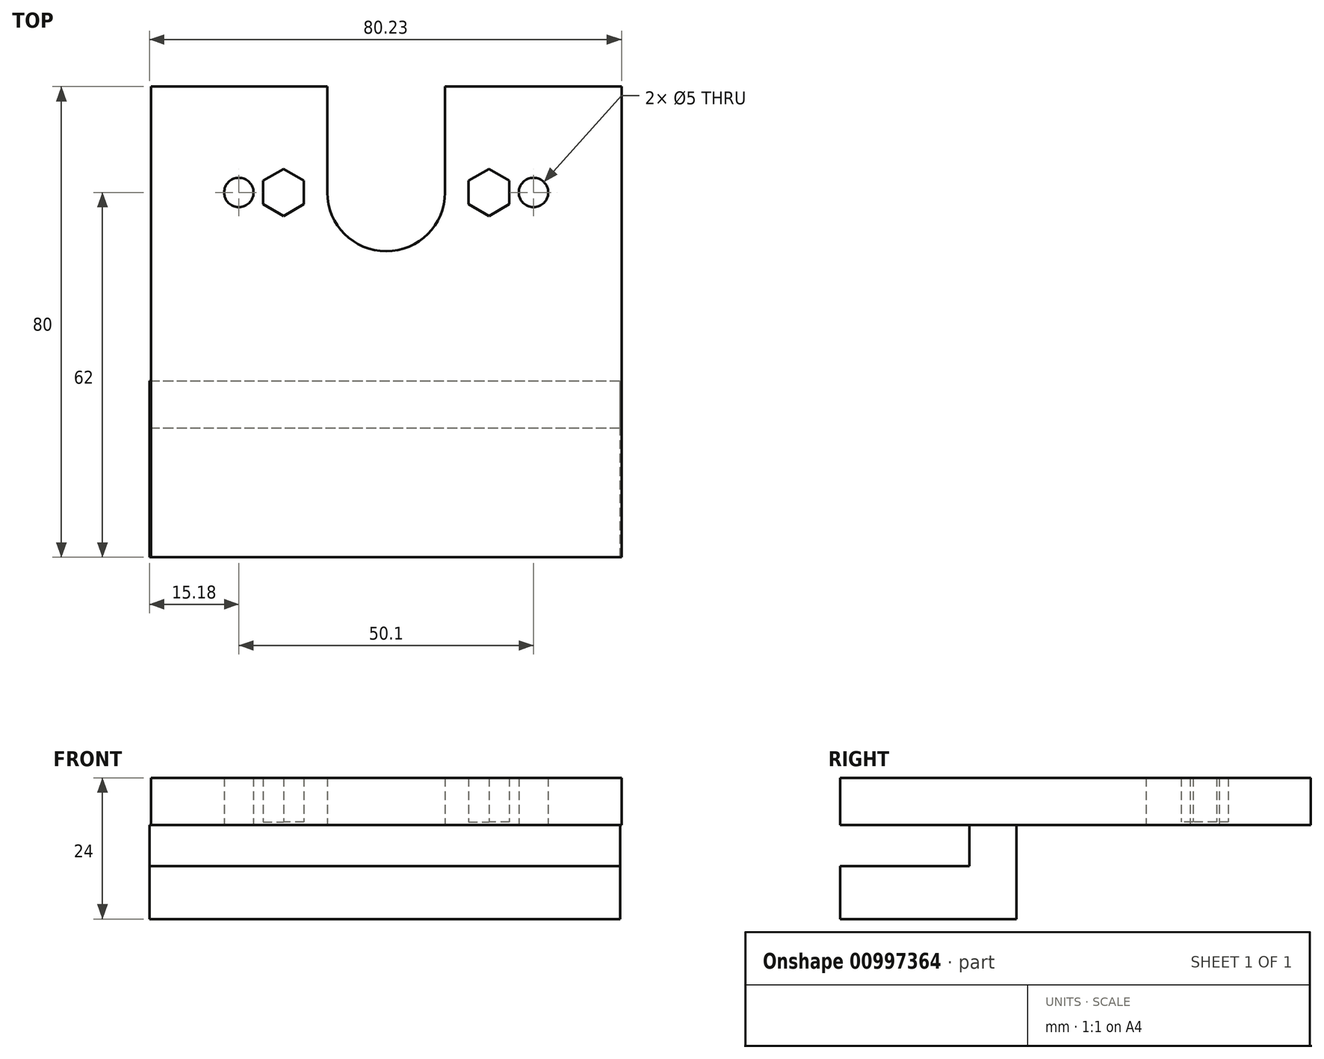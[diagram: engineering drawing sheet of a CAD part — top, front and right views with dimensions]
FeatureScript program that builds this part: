
annotation { "Feature Type Name" : "Feature", "Feature Type Description" : "" }
export const myFeature = defineFeature(function(context is Context, id is Id, definition is map)
    precondition{}
    {
        {
            var Q0;
            Q0=qCreatedBy(makeId("Top.planeOp"),FACE);
            var sketch = newSketch(context, id + "F0", { "sketchPlane" : qUnion([Q0])});
            skLineSegment(sketch, "E0.top", {"start": v(40.25, 40) * mm, "end": v(10, 40) * mm});
            skPoint(sketch, "E0.middle", {"position": v(0, 0) * mm});
            skLineSegment(sketch, "E1.MirrorCS", {"start": v(-40, 40) * mm, "end": v(-10, 40) * mm});
            skLineSegment(sketch, "E2", {"start": v(10, 40) * mm, "end": v(10, 22) * mm});
            skLineSegment(sketch, "E3.MirrorCS", {"start": v(-10, 40) * mm, "end": v(-10, 22) * mm});
            skArc(sketch, "E4", {"start": v(-10, 22) * mm, "mid": v(0, 12) * mm, "end": v(10, 22) * mm});
            skPoint(sketch, "E5", {"position": v(25.05, 22) * mm});
            skPoint(sketch, "E6", {"position": v(17.46, 22) * mm});
            skPoint(sketch, "E7.MirrorP", {"position": v(-17.46, 22) * mm});
            skPoint(sketch, "E8.MirrorP", {"position": v(-25.05, 22) * mm});
            skLineSegment(sketch, "E9", {"start": v(-40, 40) * mm, "end": v(-40, -40) * mm});
            skLineSegment(sketch, "E10.MirrorCS", {"start": v(40, 40) * mm, "end": v(40, -40) * mm});
            skLineSegment(sketch, "E11", {"start": v(-40, -40) * mm, "end": v(40, -40) * mm});
            skSolve(sketch);
        }
        {
            var Q0;
            Q0 = qSketchRegion(id + "F0", true);
            extrude(context, id + "F1", {"entities" : qUnion([Q0]), "depth" : 8 * mm, "offsetDistance" : 25 * mm});
        }
        {
            var Q0;
            Q0=sQuery(id+"F0.wireOp",VERTEX,"E5");
            var Q1;
            Q1=makeQuery(id+"F1.opExtrude","SWEPT_BODY",BODY,{"disambiguationData":[OSD([sQuery(id+"F0.wireOp",EDGE,"E0.top"),sQuery(id+"F0.wireOp",EDGE,"E1.MirrorCS"),sQuery(id+"F0.wireOp",EDGE,"E2"),sQuery(id+"F0.wireOp",EDGE,"E3.MirrorCS"),sQuery(id+"F0.wireOp",EDGE,"E4"),sQuery(id+"F0.wireOp",EDGE,"9f457f28-b589-4e44-85d8-e6faa38afad9"),sQuery(id+"F0.wireOp",EDGE,"d04040d8-0d85-434a-9426-19c5aca7a986"),sQuery(id+"F0.wireOp",EDGE,"XwE4FMA8-GxFN-yl6x-s7Xw-O0s0oBugfnyy")])]});
            hole(context, id + "F2", {"style" : HoleStyle.SIMPLE, "endStyle" : HoleEndStyle.THROUGH, "oppositeDirection" : true, "holeDiameter" : 5 * mm, "majorDiameter" : 5 * mm, "isTappedThrough" : true, "tappedDepth" : 12 * mm, "tapClearance" : 3, "startFromSketch" : true, "locations" : qUnion([Q0]), "scope" : qUnion([Q1])});
        }
        {
            var Q0;
            Q0=sQuery(id+"F0.wireOp",VERTEX,"E8.MirrorP");
            var Q1;
            Q1=makeQuery(id+"F1.opExtrude","SWEPT_BODY",BODY,{"disambiguationData":[OSD([sQuery(id+"F0.wireOp",EDGE,"E0.top"),sQuery(id+"F0.wireOp",EDGE,"E1.MirrorCS"),sQuery(id+"F0.wireOp",EDGE,"E2"),sQuery(id+"F0.wireOp",EDGE,"E3.MirrorCS"),sQuery(id+"F0.wireOp",EDGE,"E4"),sQuery(id+"F0.wireOp",EDGE,"9f457f28-b589-4e44-85d8-e6faa38afad9"),sQuery(id+"F0.wireOp",EDGE,"d04040d8-0d85-434a-9426-19c5aca7a986"),sQuery(id+"F0.wireOp",EDGE,"XwE4FMA8-GxFN-yl6x-s7Xw-O0s0oBugfnyy")])]});
            hole(context, id + "F3", {"style" : HoleStyle.SIMPLE, "endStyle" : HoleEndStyle.THROUGH, "oppositeDirection" : true, "holeDiameter" : 5 * mm, "majorDiameter" : 5 * mm, "isTappedThrough" : true, "tappedDepth" : 12 * mm, "tapClearance" : 3, "startFromSketch" : true, "locations" : qUnion([Q0]), "scope" : qUnion([Q1])});
        }
        {
            var Q0;
            Q0=makeQuery(id+"F1.opExtrude","CAP_FACE",FACE,{"disambiguationData":[OSD([sQuery(id+"F0.wireOp",EDGE,"E0.top"),sQuery(id+"F0.wireOp",EDGE,"E1.MirrorCS"),sQuery(id+"F0.wireOp",EDGE,"E2"),sQuery(id+"F0.wireOp",EDGE,"E3.MirrorCS"),sQuery(id+"F0.wireOp",EDGE,"E4"),sQuery(id+"F0.wireOp",EDGE,"9f457f28-b589-4e44-85d8-e6faa38afad9"),sQuery(id+"F0.wireOp",EDGE,"d04040d8-0d85-434a-9426-19c5aca7a986"),sQuery(id+"F0.wireOp",EDGE,"XwE4FMA8-GxFN-yl6x-s7Xw-O0s0oBugfnyy")])],"isStart":false});
            var sketch = newSketch(context, id + "F4", { "sketchPlane" : qUnion([Q0])});
            skCircle(sketch, "E12.cCircle", {"center": v(-17.46, 22) * mm, "radius": 3.46 * mm, "construction": true});
            skLineSegment(sketch, "E12.0", {"start": v(-14, 20) * mm, "end": v(-17.46, 18) * mm});
            skLineSegment(sketch, "E12.1", {"start": v(-17.46, 18) * mm, "end": v(-20.93, 20) * mm});
            skLineSegment(sketch, "E12.2", {"start": v(-20.93, 20) * mm, "end": v(-20.93, 24) * mm});
            skLineSegment(sketch, "E12.3", {"start": v(-20.93, 24) * mm, "end": v(-17.46, 26) * mm});
            skLineSegment(sketch, "E12.4", {"start": v(-17.46, 26) * mm, "end": v(-14, 24) * mm});
            skLineSegment(sketch, "E12.5", {"start": v(-14, 24) * mm, "end": v(-14, 20) * mm});
            skPoint(sketch, "E12.0.midPoint", {"position": v(-15.73, 19) * mm});
            skCircle(sketch, "E13.cCircle", {"center": v(17.46, 22) * mm, "radius": 3.46 * mm, "construction": true});
            skLineSegment(sketch, "E13.0", {"start": v(20.93, 20) * mm, "end": v(17.46, 18) * mm});
            skLineSegment(sketch, "E13.1", {"start": v(17.46, 18) * mm, "end": v(14, 20) * mm});
            skLineSegment(sketch, "E13.2", {"start": v(14, 20) * mm, "end": v(14, 24) * mm});
            skLineSegment(sketch, "E13.3", {"start": v(14, 24) * mm, "end": v(17.46, 26) * mm});
            skLineSegment(sketch, "E13.4", {"start": v(17.46, 26) * mm, "end": v(20.93, 24) * mm});
            skLineSegment(sketch, "E13.5", {"start": v(20.93, 24) * mm, "end": v(20.93, 20) * mm});
            skPoint(sketch, "E13.0.midPoint", {"position": v(19.2, 19) * mm});
            skSolve(sketch);
        }
        {
            var Q0;
            Q0 = qSketchRegion(id + "F4", true);
            extrude(context, id + "F5", {"entities" : qUnion([Q0]), "endBound" : BoundingType.SYMMETRIC, "depth" : 15 * mm, "offsetDistance" : 25 * mm});
        }
        {
            var Q0;
            Q0=makeQuery(id+"F5.opExtrude","SWEPT_BODY",BODY,{"disambiguationData":[OSD([sQuery(id+"F4.wireOp",EDGE,"E12.0"),sQuery(id+"F4.wireOp",EDGE,"E12.1"),sQuery(id+"F4.wireOp",EDGE,"E12.2"),sQuery(id+"F4.wireOp",EDGE,"E12.3"),sQuery(id+"F4.wireOp",EDGE,"E12.4"),sQuery(id+"F4.wireOp",EDGE,"E12.5")])]});
            var Q1;
            Q1=makeQuery(id+"F5.opExtrude","SWEPT_BODY",BODY,{"disambiguationData":[OSD([sQuery(id+"F4.wireOp",EDGE,"E13.0"),sQuery(id+"F4.wireOp",EDGE,"E13.1"),sQuery(id+"F4.wireOp",EDGE,"E13.2"),sQuery(id+"F4.wireOp",EDGE,"E13.3"),sQuery(id+"F4.wireOp",EDGE,"E13.4"),sQuery(id+"F4.wireOp",EDGE,"E13.5")])]});
            var Q2;
            Q2=makeQuery(id+"F1.opExtrude","SWEPT_BODY",BODY,{"disambiguationData":[OSD([sQuery(id+"F0.wireOp",EDGE,"E0.top"),sQuery(id+"F0.wireOp",EDGE,"E1.MirrorCS"),sQuery(id+"F0.wireOp",EDGE,"E2"),sQuery(id+"F0.wireOp",EDGE,"E3.MirrorCS"),sQuery(id+"F0.wireOp",EDGE,"E4"),sQuery(id+"F0.wireOp",EDGE,"9f457f28-b589-4e44-85d8-e6faa38afad9"),sQuery(id+"F0.wireOp",EDGE,"d04040d8-0d85-434a-9426-19c5aca7a986"),sQuery(id+"F0.wireOp",EDGE,"XwE4FMA8-GxFN-yl6x-s7Xw-O0s0oBugfnyy")])]});
            booleanBodies(context, id + "F6", {"operationType" : BooleanOperationType.SUBTRACTION, "tools" : qUnion([Q0, Q1]), "targets" : qUnion([Q2])});
        }
        {
            var Q0;
            Q0=makeQuery(id+"F0.imprint","IMPRINT",FACE,{"disambiguationData":[TD([[makeQuery(id+"F0.imprint","IMPRINT",EDGE,{"derivedFrom":sQuery(id+"F0.wireOp",EDGE,"E1.MirrorCS")}),-1.0]])]});
            var sketch = newSketch(context, id + "F7", { "sketchPlane" : qUnion([Q0])});
            skLineSegment(sketch, "E14.bottom", {"start": v(-40.23, -18) * mm, "end": v(39.77, -18) * mm});
            skLineSegment(sketch, "E14.top", {"start": v(-40.23, -10) * mm, "end": v(39.77, -10) * mm});
            skLineSegment(sketch, "E14.left", {"start": v(-40.23, -18) * mm, "end": v(-40.23, -10) * mm});
            skLineSegment(sketch, "E14.right", {"start": v(39.77, -18) * mm, "end": v(39.77, -10) * mm});
            skSolve(sketch);
        }
        {
            var Q0;
            Q0 = qSketchRegion(id + "F7", true);
            extrude(context, id + "F8", {"entities" : qUnion([Q0]), "operationType" : NewBodyOperationType.ADD, "oppositeDirection" : true, "depth" : 7 * mm, "offsetDistance" : 25 * mm});
        }
        {
            var Q0;
            Q0=makeQuery(id+"F8.opExtrude","CAP_FACE",FACE,{"disambiguationData":[OSD([sQuery(id+"F7.wireOp",EDGE,"E14.bottom"),sQuery(id+"F7.wireOp",EDGE,"E14.top"),sQuery(id+"F7.wireOp",EDGE,"E14.left"),sQuery(id+"F7.wireOp",EDGE,"E14.right")])],"isStart":false});
            var sketch = newSketch(context, id + "F9", { "sketchPlane" : qUnion([Q0])});
            skLineSegment(sketch, "E15.bottom", {"start": v(-40.23, 40) * mm, "end": v(39.77, 40) * mm});
            skLineSegment(sketch, "E15.top", {"start": v(-40.23, 10) * mm, "end": v(39.77, 10) * mm});
            skLineSegment(sketch, "E15.left", {"start": v(-40.23, 40) * mm, "end": v(-40.23, 10) * mm});
            skLineSegment(sketch, "E15.right", {"start": v(39.77, 40) * mm, "end": v(39.77, 10) * mm});
            skSolve(sketch);
        }
        {
            var Q0;
            Q0 = qSketchRegion(id + "F9", true);
            extrude(context, id + "F10", {"entities" : qUnion([Q0]), "operationType" : NewBodyOperationType.ADD, "depth" : 9 * mm, "offsetDistance" : 25 * mm});
        }
    });
